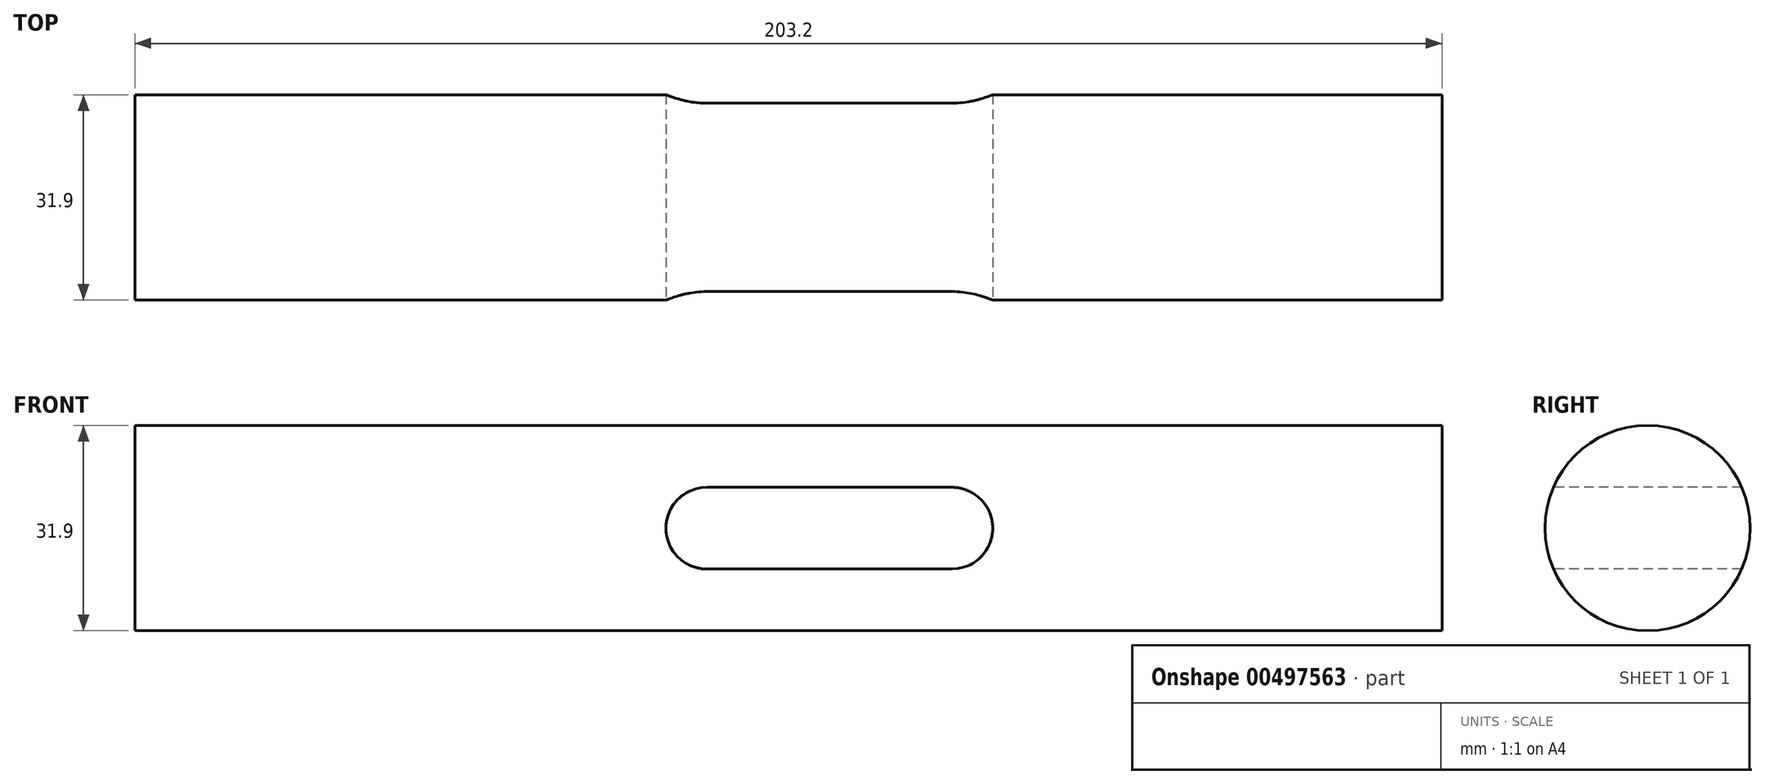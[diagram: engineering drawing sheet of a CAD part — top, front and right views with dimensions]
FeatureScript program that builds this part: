
annotation { "Feature Type Name" : "Feature", "Feature Type Description" : "" }
export const myFeature = defineFeature(function(context is Context, id is Id, definition is map)
    precondition{}
    {
        {
            var Q0;
            Q0=qCreatedBy(makeId("Right.planeOp"),FACE);
            var sketch = newSketch(context, id + "F0", { "sketchPlane" : qUnion([Q0])});
            skCircle(sketch, "E0", {"center": v(15.95, 0) * mm, "radius": 15.95 * mm});
            skSolve(sketch);
        }
        {
            var Q0;
            Q0 = qSketchRegion(id + "F0", true);
            extrude(context, id + "F1", {"entities" : qUnion([Q0]), "depth" : 203.2 * mm});
        }
        {
            var Q0;
            Q0=qCreatedBy(makeId("Front.planeOp"),FACE);
            var sketch = newSketch(context, id + "F2", { "sketchPlane" : qUnion([Q0])});
            skLineSegment(sketch, "E1", {"start": v(0, 0) * mm, "end": v(88.9, 0) * mm, "construction": true});
            skArc(sketch, "E2", {"start": v(88.9, 6.35) * mm, "mid": v(82.55, 0) * mm, "end": v(88.9, -6.35) * mm});
            skLineSegment(sketch, "E3", {"start": v(88.9, 0) * mm, "end": v(127, 0) * mm, "construction": true});
            skArc(sketch, "E4", {"start": v(127, -6.35) * mm, "mid": v(133.35, 0) * mm, "end": v(127, 6.35) * mm});
            skLineSegment(sketch, "E5", {"start": v(88.9, 6.35) * mm, "end": v(127, 6.35) * mm});
            skLineSegment(sketch, "E6", {"start": v(88.9, -6.35) * mm, "end": v(127, -6.35) * mm});
            skSolve(sketch);
        }
        {
            var Q0;
            Q0=makeQuery(id+"F2.imprint","IMPRINT",FACE,{"disambiguationData":[TD([[makeQuery(id+"F2.imprint","IMPRINT",EDGE,{"derivedFrom":sQuery(id+"F2.wireOp",EDGE,"E2")}),1.0]])]});
            extrude(context, id + "F3", {"entities" : qUnion([Q0]), "operationType" : NewBodyOperationType.REMOVE, "oppositeDirection" : true, "depth" : 31.9 * mm});
        }
    });
